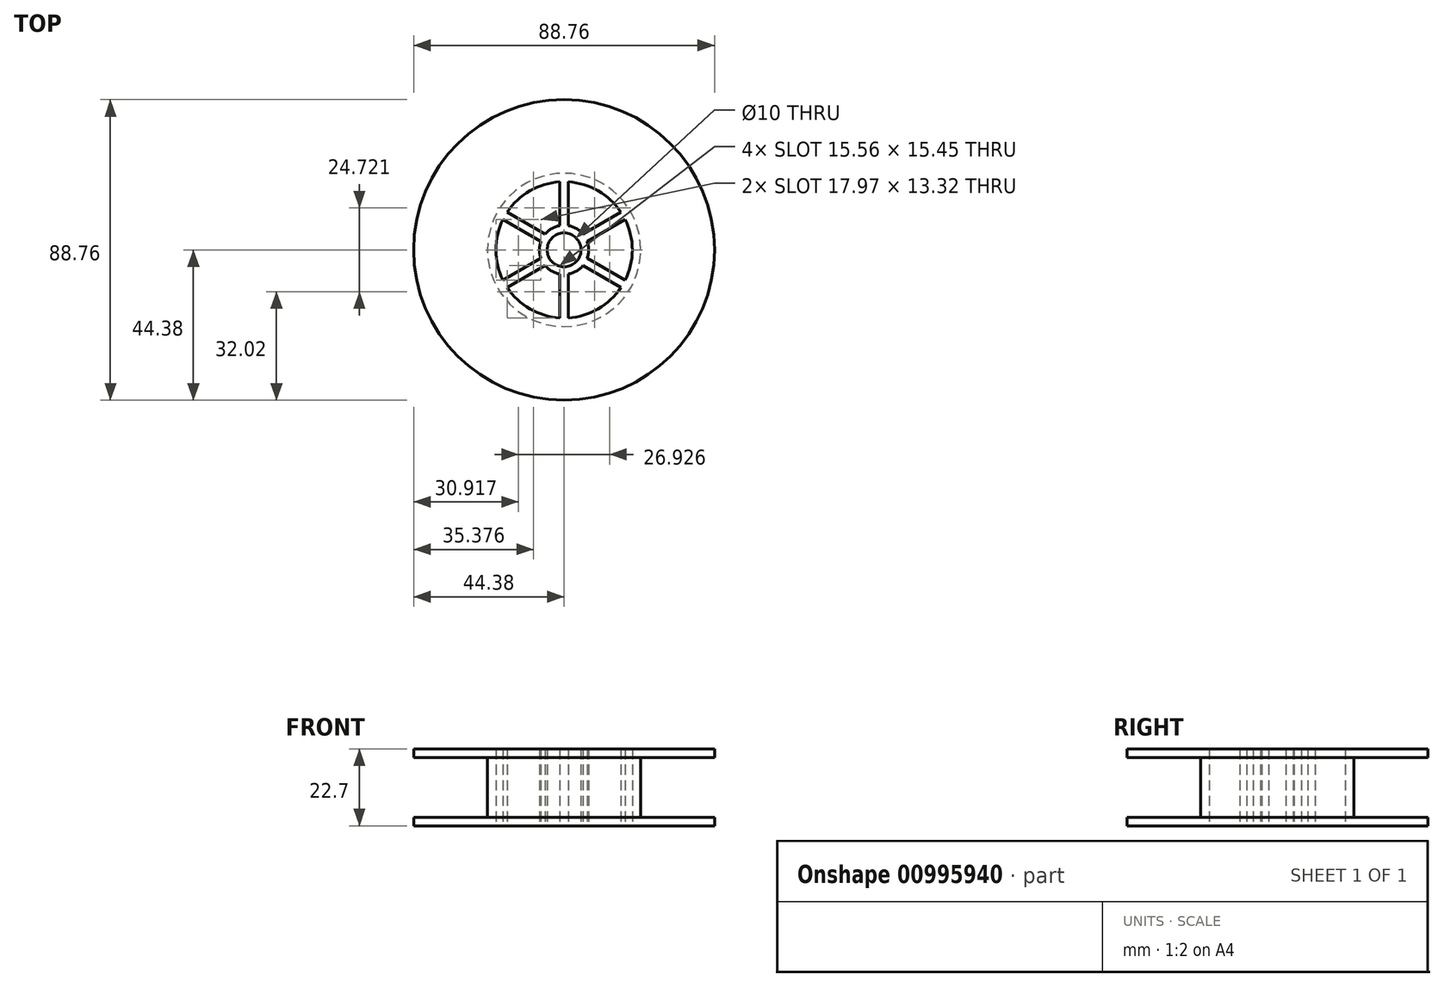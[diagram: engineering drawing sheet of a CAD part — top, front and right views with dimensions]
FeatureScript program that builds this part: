
annotation { "Feature Type Name" : "Feature", "Feature Type Description" : "" }
export const myFeature = defineFeature(function(context is Context, id is Id, definition is map)
    precondition{}
    {
        {
            var Q0;
            Q0=qCreatedBy(makeId("Top.planeOp"),FACE);
            var sketch = newSketch(context, id + "F0", { "sketchPlane" : qUnion([Q0])});
            skCircle(sketch, "E0", {"center": v(0, 0) * mm, "radius": 44.38 * mm});
            skCircle(sketch, "E1", {"center": v(0, 0) * mm, "radius": 20.12 * mm});
            skCircle(sketch, "E2", {"center": v(0, 0) * mm, "radius": 5 * mm});
            skLineSegment(sketch, "E3.bottom", {"start": v(-1.22, 3.17) * mm, "end": v(1.22, 3.17) * mm});
            skLineSegment(sketch, "E3.top", {"start": v(-1.22, 21.63) * mm, "end": v(1.22, 21.63) * mm});
            skLineSegment(sketch, "E3.left", {"start": v(-1.22, 3.17) * mm, "end": v(-1.22, 21.63) * mm});
            skLineSegment(sketch, "E3.right", {"start": v(1.22, 3.17) * mm, "end": v(1.22, 21.63) * mm});
            skLineSegment(sketch, "E4", {"start": v(0, 0) * mm, "end": v(0, 23.39) * mm, "construction": true});
            skLineSegment(sketch, "E5.1.0", {"start": v(-3.36, 0.52) * mm, "end": v(-19.34, 9.75) * mm});
            skLineSegment(sketch, "E5.1.1", {"start": v(-19.34, 9.75) * mm, "end": v(-18.12, 11.87) * mm});
            skLineSegment(sketch, "E5.1.2", {"start": v(-2.13, 2.64) * mm, "end": v(-18.12, 11.87) * mm});
            skLineSegment(sketch, "E5.1.3", {"start": v(-3.36, 0.52) * mm, "end": v(-2.13, 2.64) * mm});
            skLineSegment(sketch, "E5.2.0", {"start": v(-2.13, -2.64) * mm, "end": v(-18.12, -11.87) * mm});
            skLineSegment(sketch, "E5.2.1", {"start": v(-18.12, -11.87) * mm, "end": v(-19.34, -9.75) * mm});
            skLineSegment(sketch, "E5.2.2", {"start": v(-3.36, -0.52) * mm, "end": v(-19.34, -9.75) * mm});
            skLineSegment(sketch, "E5.2.3", {"start": v(-2.13, -2.64) * mm, "end": v(-3.36, -0.52) * mm});
            skLineSegment(sketch, "E5.3.0", {"start": v(1.22, -3.17) * mm, "end": v(1.22, -21.63) * mm});
            skLineSegment(sketch, "E5.3.1", {"start": v(1.22, -21.63) * mm, "end": v(-1.22, -21.63) * mm});
            skLineSegment(sketch, "E5.3.2", {"start": v(-1.22, -3.17) * mm, "end": v(-1.22, -21.63) * mm});
            skLineSegment(sketch, "E5.3.3", {"start": v(1.22, -3.17) * mm, "end": v(-1.22, -3.17) * mm});
            skLineSegment(sketch, "E5.4.0", {"start": v(3.36, -0.52) * mm, "end": v(19.34, -9.75) * mm});
            skLineSegment(sketch, "E5.4.1", {"start": v(19.34, -9.75) * mm, "end": v(18.12, -11.87) * mm});
            skLineSegment(sketch, "E5.4.2", {"start": v(2.13, -2.64) * mm, "end": v(18.12, -11.87) * mm});
            skLineSegment(sketch, "E5.4.3", {"start": v(3.36, -0.52) * mm, "end": v(2.13, -2.64) * mm});
            skLineSegment(sketch, "E5.5.0", {"start": v(2.13, 2.64) * mm, "end": v(18.12, 11.87) * mm});
            skLineSegment(sketch, "E5.5.1", {"start": v(18.12, 11.87) * mm, "end": v(19.34, 9.75) * mm});
            skLineSegment(sketch, "E5.5.2", {"start": v(3.36, 0.52) * mm, "end": v(19.34, 9.75) * mm});
            skLineSegment(sketch, "E5.5.3", {"start": v(2.13, 2.64) * mm, "end": v(3.36, 0.52) * mm});
            skCircle(sketch, "E6", {"center": v(0, 0) * mm, "radius": 7.25 * mm});
            skSolve(sketch);
        }
        {
            var Q0;
            Q0 = qSketchRegion(id + "F0", true);
            var Q1;
            {var subQ0=sQuery(id+"F0.wireOp",EDGE,"E5.1.2");var subQ1=sQuery(id+"F0.wireOp",EDGE,"E1");var subQ2=makeQuery(id+"F0.imprint","INTERSECT",VERTEX,{"derivedFrom":[subQ1,subQ0]});Q1=makeQuery(id+"F0.imprint","IMPRINT",FACE,{"disambiguationData":[TD([[makeQuery(id+"F0.imprint","IMPRINT",EDGE,{"disambiguationData":[TD([[subQ2,-1.0]])],"derivedFrom":subQ1}),1.0]])]});}
            var Q2;
            {var subQ0=sQuery(id+"F0.wireOp",EDGE,"E3.right");var subQ1=sQuery(id+"F0.wireOp",EDGE,"E1");var subQ2=makeQuery(id+"F0.imprint","INTERSECT",VERTEX,{"derivedFrom":[subQ1,subQ0]});Q2=makeQuery(id+"F0.imprint","IMPRINT",FACE,{"disambiguationData":[TD([[makeQuery(id+"F0.imprint","IMPRINT",EDGE,{"disambiguationData":[TD([[subQ2,-1.0]])],"derivedFrom":subQ1}),1.0]])]});}
            var Q3;
            {var subQ0=sQuery(id+"F0.wireOp",EDGE,"E5.5.0");var subQ1=sQuery(id+"F0.wireOp",EDGE,"E1");var subQ2=makeQuery(id+"F0.imprint","INTERSECT",VERTEX,{"derivedFrom":[subQ1,subQ0]});Q3=makeQuery(id+"F0.imprint","IMPRINT",FACE,{"disambiguationData":[TD([[makeQuery(id+"F0.imprint","IMPRINT",EDGE,{"disambiguationData":[TD([[subQ2,1.0]])],"derivedFrom":subQ1}),1.0]])]});}
            var Q4;
            {var subQ0=sQuery(id+"F0.wireOp",EDGE,"E5.4.2");var subQ1=sQuery(id+"F0.wireOp",EDGE,"E1");var subQ2=makeQuery(id+"F0.imprint","INTERSECT",VERTEX,{"derivedFrom":[subQ1,subQ0]});Q4=makeQuery(id+"F0.imprint","IMPRINT",FACE,{"disambiguationData":[TD([[makeQuery(id+"F0.imprint","IMPRINT",EDGE,{"disambiguationData":[TD([[subQ2,-1.0]])],"derivedFrom":subQ1}),1.0]])]});}
            var Q5;
            {var subQ0=sQuery(id+"F0.wireOp",EDGE,"E5.2.2");var subQ1=sQuery(id+"F0.wireOp",EDGE,"E1");var subQ2=makeQuery(id+"F0.imprint","INTERSECT",VERTEX,{"derivedFrom":[subQ1,subQ0]});Q5=makeQuery(id+"F0.imprint","IMPRINT",FACE,{"disambiguationData":[TD([[makeQuery(id+"F0.imprint","IMPRINT",EDGE,{"disambiguationData":[TD([[subQ2,-1.0]])],"derivedFrom":subQ1}),1.0]])]});}
            var Q6;
            {var subQ0=sQuery(id+"F0.wireOp",EDGE,"E5.3.2");var subQ1=sQuery(id+"F0.wireOp",EDGE,"E1");var subQ2=makeQuery(id+"F0.imprint","INTERSECT",VERTEX,{"derivedFrom":[subQ1,subQ0]});Q6=makeQuery(id+"F0.imprint","IMPRINT",FACE,{"disambiguationData":[TD([[makeQuery(id+"F0.imprint","IMPRINT",EDGE,{"disambiguationData":[TD([[subQ2,-1.0]])],"derivedFrom":subQ1}),1.0]])]});}
            var Q7;
            {var subQ5=sQuery(id+"F0.wireOp",EDGE,"E5.1.1");Q7=makeQuery(id+"F0.imprint","IMPRINT",FACE,{"disambiguationData":[TD([[makeQuery(id+"F0.imprint","IMPRINT",EDGE,{"derivedFrom":subQ5}),-1.0]])]});}
            var Q8;
            {var subQ5=sQuery(id+"F0.wireOp",EDGE,"E3.top");Q8=makeQuery(id+"F0.imprint","IMPRINT",FACE,{"disambiguationData":[TD([[makeQuery(id+"F0.imprint","IMPRINT",EDGE,{"derivedFrom":subQ5}),-1.0]])]});}
            var Q9;
            {var subQ5=sQuery(id+"F0.wireOp",EDGE,"E5.5.1");Q9=makeQuery(id+"F0.imprint","IMPRINT",FACE,{"disambiguationData":[TD([[makeQuery(id+"F0.imprint","IMPRINT",EDGE,{"derivedFrom":subQ5}),-1.0]])]});}
            var Q10;
            {var subQ5=sQuery(id+"F0.wireOp",EDGE,"E5.4.1");Q10=makeQuery(id+"F0.imprint","IMPRINT",FACE,{"disambiguationData":[TD([[makeQuery(id+"F0.imprint","IMPRINT",EDGE,{"derivedFrom":subQ5}),-1.0]])]});}
            var Q11;
            {var subQ5=sQuery(id+"F0.wireOp",EDGE,"E5.3.1");Q11=makeQuery(id+"F0.imprint","IMPRINT",FACE,{"disambiguationData":[TD([[makeQuery(id+"F0.imprint","IMPRINT",EDGE,{"derivedFrom":subQ5}),-1.0]])]});}
            var Q12;
            {var subQ5=sQuery(id+"F0.wireOp",EDGE,"E5.2.1");Q12=makeQuery(id+"F0.imprint","IMPRINT",FACE,{"disambiguationData":[TD([[makeQuery(id+"F0.imprint","IMPRINT",EDGE,{"derivedFrom":subQ5}),-1.0]])]});}
            var Q13;
            {var subQ0=sQuery(id+"F0.wireOp",EDGE,"E5.1.2");var subQ1=sQuery(id+"F0.wireOp",EDGE,"E2");var subQ2=makeQuery(id+"F0.imprint","INTERSECT",VERTEX,{"derivedFrom":[subQ1,subQ0]});Q13=makeQuery(id+"F0.imprint","IMPRINT",FACE,{"disambiguationData":[TD([[makeQuery(id+"F0.imprint","IMPRINT",EDGE,{"disambiguationData":[TD([[subQ2,-1.0]])],"derivedFrom":subQ1}),-1.0]])]});}
            var Q14;
            {var subQ0=sQuery(id+"F0.wireOp",EDGE,"E5.1.0");var subQ1=sQuery(id+"F0.wireOp",EDGE,"E2");var subQ2=makeQuery(id+"F0.imprint","INTERSECT",VERTEX,{"derivedFrom":[subQ1,subQ0]});Q14=makeQuery(id+"F0.imprint","IMPRINT",FACE,{"disambiguationData":[TD([[makeQuery(id+"F0.imprint","IMPRINT",EDGE,{"disambiguationData":[TD([[subQ2,-1.0]])],"derivedFrom":subQ1}),-1.0]])]});}
            var Q15;
            {var subQ0=sQuery(id+"F0.wireOp",EDGE,"E5.2.2");var subQ1=sQuery(id+"F0.wireOp",EDGE,"E2");var subQ2=makeQuery(id+"F0.imprint","INTERSECT",VERTEX,{"derivedFrom":[subQ1,subQ0]});Q15=makeQuery(id+"F0.imprint","IMPRINT",FACE,{"disambiguationData":[TD([[makeQuery(id+"F0.imprint","IMPRINT",EDGE,{"disambiguationData":[TD([[subQ2,-1.0]])],"derivedFrom":subQ1}),-1.0]])]});}
            var Q16;
            {var subQ0=sQuery(id+"F0.wireOp",EDGE,"E5.2.0");var subQ1=sQuery(id+"F0.wireOp",EDGE,"E2");var subQ2=makeQuery(id+"F0.imprint","INTERSECT",VERTEX,{"derivedFrom":[subQ1,subQ0]});Q16=makeQuery(id+"F0.imprint","IMPRINT",FACE,{"disambiguationData":[TD([[makeQuery(id+"F0.imprint","IMPRINT",EDGE,{"disambiguationData":[TD([[subQ2,-1.0]])],"derivedFrom":subQ1}),-1.0]])]});}
            var Q17;
            {var subQ0=sQuery(id+"F0.wireOp",EDGE,"E5.3.2");var subQ1=sQuery(id+"F0.wireOp",EDGE,"E2");var subQ2=makeQuery(id+"F0.imprint","INTERSECT",VERTEX,{"derivedFrom":[subQ1,subQ0]});Q17=makeQuery(id+"F0.imprint","IMPRINT",FACE,{"disambiguationData":[TD([[makeQuery(id+"F0.imprint","IMPRINT",EDGE,{"disambiguationData":[TD([[subQ2,-1.0]])],"derivedFrom":subQ1}),-1.0]])]});}
            var Q18;
            {var subQ0=sQuery(id+"F0.wireOp",EDGE,"E5.4.2");var subQ1=sQuery(id+"F0.wireOp",EDGE,"E2");var subQ2=makeQuery(id+"F0.imprint","INTERSECT",VERTEX,{"derivedFrom":[subQ1,subQ0]});Q18=makeQuery(id+"F0.imprint","IMPRINT",FACE,{"disambiguationData":[TD([[makeQuery(id+"F0.imprint","IMPRINT",EDGE,{"disambiguationData":[TD([[subQ2,-1.0]])],"derivedFrom":subQ1}),-1.0]])]});}
            var Q19;
            {var subQ0=sQuery(id+"F0.wireOp",EDGE,"E5.5.2");var subQ1=sQuery(id+"F0.wireOp",EDGE,"E2");var subQ2=makeQuery(id+"F0.imprint","INTERSECT",VERTEX,{"derivedFrom":[subQ1,subQ0]});Q19=makeQuery(id+"F0.imprint","IMPRINT",FACE,{"disambiguationData":[TD([[makeQuery(id+"F0.imprint","IMPRINT",EDGE,{"disambiguationData":[TD([[subQ2,1.0]])],"derivedFrom":subQ1}),-1.0]])]});}
            var Q20;
            {var subQ0=sQuery(id+"F0.wireOp",EDGE,"E5.5.0");var subQ1=sQuery(id+"F0.wireOp",EDGE,"E2");var subQ2=makeQuery(id+"F0.imprint","INTERSECT",VERTEX,{"derivedFrom":[subQ1,subQ0]});Q20=makeQuery(id+"F0.imprint","IMPRINT",FACE,{"disambiguationData":[TD([[makeQuery(id+"F0.imprint","IMPRINT",EDGE,{"disambiguationData":[TD([[subQ2,1.0]])],"derivedFrom":subQ1}),-1.0]])]});}
            var Q21;
            {var subQ0=sQuery(id+"F0.wireOp",EDGE,"E5.5.0");var subQ1=sQuery(id+"F0.wireOp",EDGE,"E2");var subQ2=makeQuery(id+"F0.imprint","INTERSECT",VERTEX,{"derivedFrom":[subQ1,subQ0]});Q21=makeQuery(id+"F0.imprint","IMPRINT",FACE,{"disambiguationData":[TD([[makeQuery(id+"F0.imprint","IMPRINT",EDGE,{"disambiguationData":[TD([[subQ2,-1.0]])],"derivedFrom":subQ1}),-1.0]])]});}
            var Q22;
            {var subQ0=sQuery(id+"F0.wireOp",EDGE,"E3.left");var subQ1=sQuery(id+"F0.wireOp",EDGE,"E2");var subQ2=makeQuery(id+"F0.imprint","INTERSECT",VERTEX,{"derivedFrom":[subQ1,subQ0]});Q22=makeQuery(id+"F0.imprint","IMPRINT",FACE,{"disambiguationData":[TD([[makeQuery(id+"F0.imprint","IMPRINT",EDGE,{"disambiguationData":[TD([[subQ2,-1.0]])],"derivedFrom":subQ1}),-1.0]])]});}
            var Q23;
            {var subQ0=sQuery(id+"F0.wireOp",EDGE,"E3.right");var subQ1=sQuery(id+"F0.wireOp",EDGE,"E2");var subQ2=makeQuery(id+"F0.imprint","INTERSECT",VERTEX,{"derivedFrom":[subQ1,subQ0]});Q23=makeQuery(id+"F0.imprint","IMPRINT",FACE,{"disambiguationData":[TD([[makeQuery(id+"F0.imprint","IMPRINT",EDGE,{"disambiguationData":[TD([[subQ2,-1.0]])],"derivedFrom":subQ1}),-1.0]])]});}
            var Q24;
            {var subQ0=sQuery(id+"F0.wireOp",EDGE,"E5.3.0");var subQ1=sQuery(id+"F0.wireOp",EDGE,"E2");var subQ2=makeQuery(id+"F0.imprint","INTERSECT",VERTEX,{"derivedFrom":[subQ1,subQ0]});Q24=makeQuery(id+"F0.imprint","IMPRINT",FACE,{"disambiguationData":[TD([[makeQuery(id+"F0.imprint","IMPRINT",EDGE,{"disambiguationData":[TD([[subQ2,-1.0]])],"derivedFrom":subQ1}),-1.0]])]});}
            extrude(context, id + "F1", {"entities" : qUnion([Q0, Q1, Q2, Q3, Q4, Q5, Q6, Q7, Q8, Q9, Q10, Q11, Q12, Q13, Q14, Q15, Q16, Q17, Q18, Q19, Q20, Q21, Q22, Q23, Q24]), "depth" : 22.7 * mm, "offsetDistance" : 25 * mm});
        }
        {
            var Q0;
            Q0=makeQuery(id+"F1.opExtrude","CAP_FACE",FACE,{"disambiguationData":[OSD([sQuery(id+"F0.wireOp",EDGE,"E0"),sQuery(id+"F0.wireOp",EDGE,"E1"),sQuery(id+"F0.wireOp",EDGE,"E2"),sQuery(id+"F0.wireOp",EDGE,"E3.left"),sQuery(id+"F0.wireOp",EDGE,"E3.right"),sQuery(id+"F0.wireOp",EDGE,"E5.1.0"),sQuery(id+"F0.wireOp",EDGE,"E5.1.2"),sQuery(id+"F0.wireOp",EDGE,"E5.2.0"),sQuery(id+"F0.wireOp",EDGE,"E5.2.2"),sQuery(id+"F0.wireOp",EDGE,"E5.3.0"),sQuery(id+"F0.wireOp",EDGE,"E5.3.2"),sQuery(id+"F0.wireOp",EDGE,"E5.4.0"),sQuery(id+"F0.wireOp",EDGE,"E5.4.2"),sQuery(id+"F0.wireOp",EDGE,"E5.5.0"),sQuery(id+"F0.wireOp",EDGE,"E5.5.2"),sQuery(id+"F0.wireOp",EDGE,"E6")])],"isStart":false});
            var sketch = newSketch(context, id + "F2", { "sketchPlane" : qUnion([Q0])});
            skCircle(sketch, "E7", {"center": v(0, 0) * mm, "radius": 20.13 * mm});
            skPoint(sketch, "E8", {"position": v(0, 44.38) * mm});
            skCircle(sketch, "E9", {"center": v(0, 0) * mm, "radius": 44.38 * mm});
            skCircle(sketch, "E10", {"center": v(0, 0) * mm, "radius": 22.63 * mm});
            skSolve(sketch);
        }
        {
            var Q0;
            Q0 = qSketchRegion(id + "F2", true);
            extrude(context, id + "F3", {"entities" : qUnion([Q0]), "operationType" : NewBodyOperationType.REMOVE, "oppositeDirection" : true, "depth" : 20.2 * mm, "offsetDistance" : 25 * mm});
        }
        {
            var Q0;
            Q0=makeQuery(id+"F1.opExtrude","CAP_FACE",FACE,{"disambiguationData":[OSD([sQuery(id+"F0.wireOp",EDGE,"E0"),sQuery(id+"F0.wireOp",EDGE,"E1"),sQuery(id+"F0.wireOp",EDGE,"E2"),sQuery(id+"F0.wireOp",EDGE,"E3.left"),sQuery(id+"F0.wireOp",EDGE,"E3.right"),sQuery(id+"F0.wireOp",EDGE,"E5.1.0"),sQuery(id+"F0.wireOp",EDGE,"E5.1.2"),sQuery(id+"F0.wireOp",EDGE,"E5.2.0"),sQuery(id+"F0.wireOp",EDGE,"E5.2.2"),sQuery(id+"F0.wireOp",EDGE,"E5.3.0"),sQuery(id+"F0.wireOp",EDGE,"E5.3.2"),sQuery(id+"F0.wireOp",EDGE,"E5.4.0"),sQuery(id+"F0.wireOp",EDGE,"E5.4.2"),sQuery(id+"F0.wireOp",EDGE,"E5.5.0"),sQuery(id+"F0.wireOp",EDGE,"E5.5.2"),sQuery(id+"F0.wireOp",EDGE,"E6")])],"isStart":false});
            var sketch = newSketch(context, id + "F4", { "sketchPlane" : qUnion([Q0])});
            skCircle(sketch, "E11.0", {"center": v(0, 0) * mm, "radius": 44.38 * mm});
            skCircle(sketch, "E12.0", {"center": v(0, 0) * mm, "radius": 22.63 * mm});
            skSolve(sketch);
        }
        {
            var Q0;
            Q0 = qSketchRegion(id + "F4", true);
            extrude(context, id + "F5", {"entities" : qUnion([Q0]), "operationType" : NewBodyOperationType.ADD, "oppositeDirection" : true, "depth" : 2.5 * mm, "offsetDistance" : 25 * mm});
        }
    });
